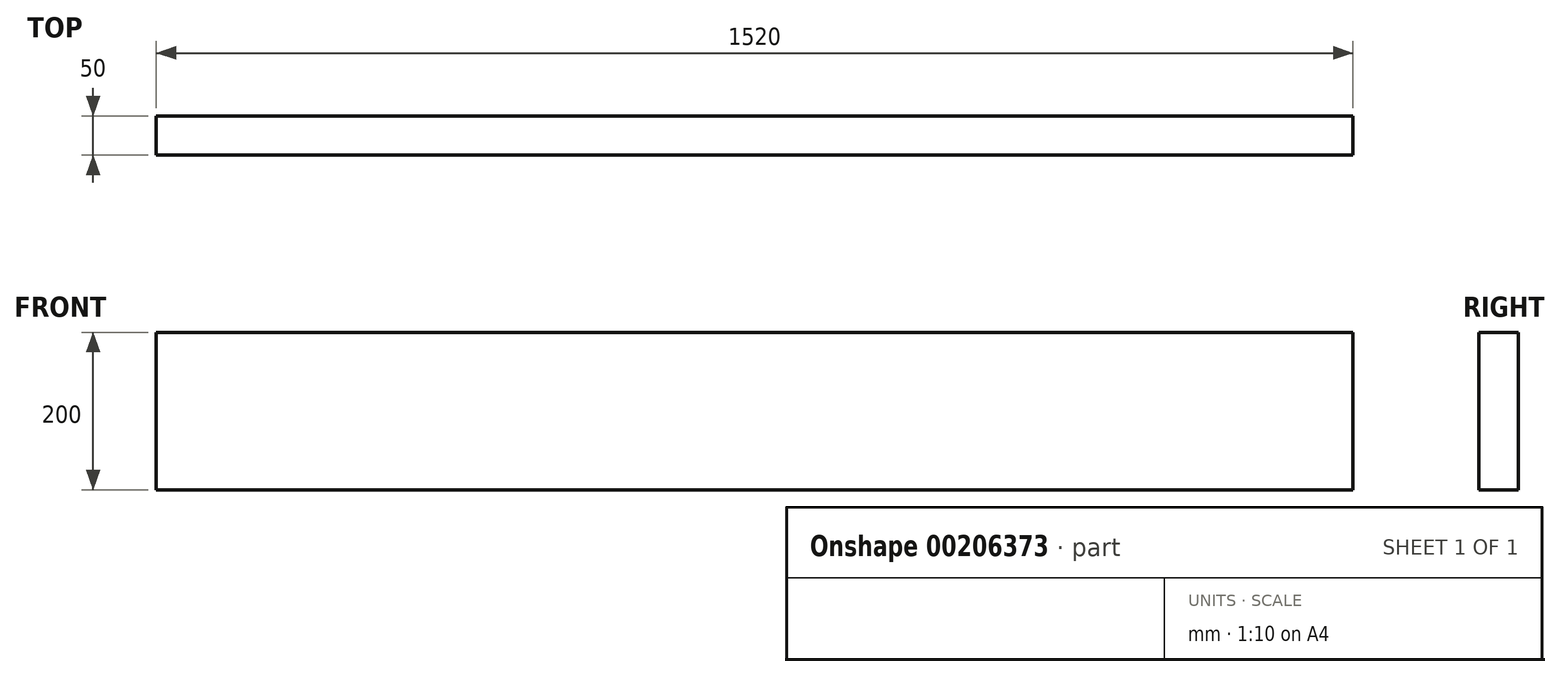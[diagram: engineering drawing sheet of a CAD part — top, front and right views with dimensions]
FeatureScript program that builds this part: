
annotation { "Feature Type Name" : "Feature", "Feature Type Description" : "" }
export const myFeature = defineFeature(function(context is Context, id is Id, definition is map)
    precondition{}
    {
        {
            var Q0;
            Q0=qCreatedBy(makeId("Top.planeOp"),FACE);
            var sketch = newSketch(context, id + "F0", { "sketchPlane" : qUnion([Q0])});
            skLineSegment(sketch, "E0.bottom", {"start": v(-22.75, -5.3) * mm, "end": v(1497.25, -5.3) * mm});
            skLineSegment(sketch, "E0.top", {"start": v(-22.75, 44.7) * mm, "end": v(1497.25, 44.7) * mm});
            skLineSegment(sketch, "E0.left", {"start": v(-22.75, -5.3) * mm, "end": v(-22.75, 44.7) * mm});
            skLineSegment(sketch, "E0.right", {"start": v(1497.25, -5.3) * mm, "end": v(1497.25, 44.7) * mm});
            skSolve(sketch);
        }
        {
            var Q0;
            Q0 = qSketchRegion(id + "F0", true);
            extrude(context, id + "F1", {"entities" : qUnion([Q0]), "depth" : 200 * mm});
        }
    });
